# Revit family: Lighting-Floodlights-GEWISS-SPATIUMPRO3-LED-FLOODLIGHT_OPTIC-ASYMMETRICAL_3MODULES
name_source: partatom
category: Apparecchi per illuminazione
units: mm (PartAtom-declared; Revit-internal decimal feet)

## family parameters
Condiviso = Sì
Host = Superficie
Punto di calcolo locali = Sì
Quota connettore circolare = Usa diametro
Sorgente d'illuminazione = Sì
Taglio con vuoti quando caricato = No
Tipo di parte = Normale

## types (12) — shared parameters
Angolo inclinazione = 60.00°
Application = Indoor / Outdoor
Body = Die-cast aluminium
Catalogue = LIGHTING
Colour = Graphite grey
Colour : = Polyester powder coated
Context = Big areas
Control System = See external supply unit
Driver = To be ordered separately
Driver Box = External
Driver failure rate = See external supply unit
Emetti da lunghezza linea = 610 mm
External screw = Stainless steel
File diagramma fotometrico = generic
Filtro dei colori = 16777215
Fixing = Bracket
Gasket = Anti-aging silicone
IDF = 03c426b5-8734-42fa-97cf-48da1bf4a1dc
IDT = 7e9d96b5-f19d-49c1-94a6-055880650604
IP degree = IP66
Immagine tipo = SPATIUMpro3.jpg
Insulation class = I
LED Maintenance = Yes
Lifetime = L90B10(Tq25°C)>100.000h; L80B10(Tq25°C)>150.000h
Lugnezza massima = 74 mm  [stored 0.242782 ft]
Luminaire = High power LED floodlight
Maximum surface exposed to the wind : = 0,36 m²
Mouting and installation = High-mast lighting - Wall mounting
Operating temperature : = -25 +50 °C
Optic : = Lens T.I.R.Ex. in PMMA HT
Optic Maintenance = Not available
Overvoltage protection = See external supply unit
POSIZIONE = 80000
Produttore = GEWISS S.p.A.
Prospetto di default = 1219 mm
Rated frequency (Hz) = See external supply unit
Shield type = Flat tempered glass 4mm
Shock resistance = IK08
Standard Deviation Colour Matching = SDCM = 5
Standard- = EN 60598-1; EN 60598-2-5; IEC/TR 62778; EN 62493
Supply voltage = See external supply unit
System power = 1200 W
Technical sheet = https://www.gewiss.com
Tilt- = Rotation on bracket with integrated goniometer
Type of light source = LED - Not replaceable
URL = https://www.gewiss.com
Unified Glare Rating = ULOR = 0%
Unique digital code (Datamatrix) = Currently not present
Variazione temperatura colore lampada con luminosità attenuata = <Nessuno>
Version file RFA = 21.9
Warranty = 5 years
Weight (kg): = 30
Wiring = Watertight connector between floodlight and supply unit
larghezza lampada = 50 mm  [stored 0.164042 ft]

## per-type parameters (varying)
| type | Color Rendering Index | Colour temperature | Descrizione | Efficiency (lm/W) | IPEA | Lumen output (lm) | Modello | Optic | Versions |
| GWP3333AB857 - SPATIUM PRO 3M CL.I A1 CRI 80 5700K | CRI 80 | 5700 K | SPATIUM PRO 3M CL.I A1 CRI 80 5700K | 99 | LARGE AREAS = A // GREEN AREAS = B | 119000 | GWP3333AB857 | Asymmetric 45° | Cold light 5700K |
| GWP3333AC830 - SPATIUM PRO 3M CL.I A2 CRI 80 3000K | CRI 80 | 3000 K | SPATIUM PRO 3M CL.I A2 CRI 80 3000K | 88 | LARGE AREAS = B // GREEN AREAS = C | 106000 | GWP3333AC830 | Asymmetric 60° | Hot light 3000K |
| GWP3333AC857 - SPATIUM PRO 3M CL.I A2 CRI 80 5700K | CRI 80 | 5700 K | SPATIUM PRO 3M CL.I A2 CRI 80 5700K | 92 | LARGE AREAS = B // GREEN AREAS = C | 110000 | GWP3333AC857 | Asymmetric 60° | Cold light 5700K |
| GWP3333AB840 - SPATIUM PRO 3M CL.I A1 CRI 80 4000K | CRI 80 | 4000 K | SPATIUM PRO 3M CL.I A1 CRI 80 4000K | 99 | LARGE AREAS = A // GREEN AREAS = B | 119000 | GWP3333AB840 | Asymmetric 45° | Natural light 4000K |
| GWP3333AC730 - SPATIUM PRO 3M CL.I A2 CRI 70 3000K | CRI70 | 3000 K | SPATIUM PRO 3M CL.I A2 CRI 70 3000K | 100 | LARGE AREAS = A // GREEN AREAS = B | 120000 | GWP3333AC730 | Asymmetric 60° | Hot light 3000K |
| GWP3333AB730 - SPATIUM PRO 3M CL.I A1 CRI 70 3000K | CRI70 | 3000 K | SPATIUM PRO 3M CL.I A1 CRI 70 3000K | 108 | LARGE AREAS = A+ // GREEN AREAS = A | 130000 | GWP3333AB730 | Asymmetric 45° | Hot light 3000K |
| GWP3333AC840 - SPATIUM PRO 3M CL.I A2 CRI 80 4000K | CRI 80 | 4000 K | SPATIUM PRO 3M CL.I A2 CRI 80 4000K | 92 | LARGE AREAS = B // GREEN AREAS = C | 110000 | GWP3333AC840 | Asymmetric 60° | Natural light 4000K |
| GWP3333AC757 - SPATIUM PRO 3M CL.I A2 CRI 70 5700K | CRI70 | 5700 K | SPATIUM PRO 3M CL.I A2 CRI 70 5700K | 106 | LARGE AREAS = A+ // GREEN AREAS = B | 127500 | GWP3333AC757 | Asymmetric 60° | Cold light 5700K |
| GWP3333AC740 - SPATIUM PRO 3M CL.I A2 CRI 70 4000K | CRI70 | 4000 K | SPATIUM PRO 3M CL.I A2 CRI 70 4000K | 106 | LARGE AREAS = A+ // GREEN AREAS = B | 127500 | GWP3333AC740 | Asymmetric 60° | Natural light 4000K |
| GWP3333AB740 - SPATIUM PRO 3M CL.I A1 CRI 70 4000K | CRI70 | 4000 K | SPATIUM PRO 3M CL.I A1 CRI 70 4000K | 115 | LARGE AREAS = A++ // GREEN AREAS = A | 138000 | GWP3333AB740 | Asymmetric 45° | Natural light 4000K |
| GWP3333AB830 - SPATIUM PRO 3M CL.I A1 CRI 80 3000K | CRI 80 | 3000 K | SPATIUM PRO 3M CL.I A1 CRI 80 3000K | 96 | LARGE AREAS = A // GREEN AREAS = C | 115000 | GWP3333AB830 | Asymmetric 45° | Hot light 3000K |
| GWP3333AB757 - SPATIUM PRO 3M CL.I A1 CRI 70 5700K | CRI70 | 5700 K | SPATIUM PRO 3M CL.I A1 CRI 70 5700K | 115 | LARGE AREAS = A++ // GREEN AREAS = A | 138000 | GWP3333AB757 | Asymmetric 45° | Cold light 5700K |

note: [stored X ft] marks values corroborated as IEEE doubles in the binary element streams (Revit-internal decimal feet)
